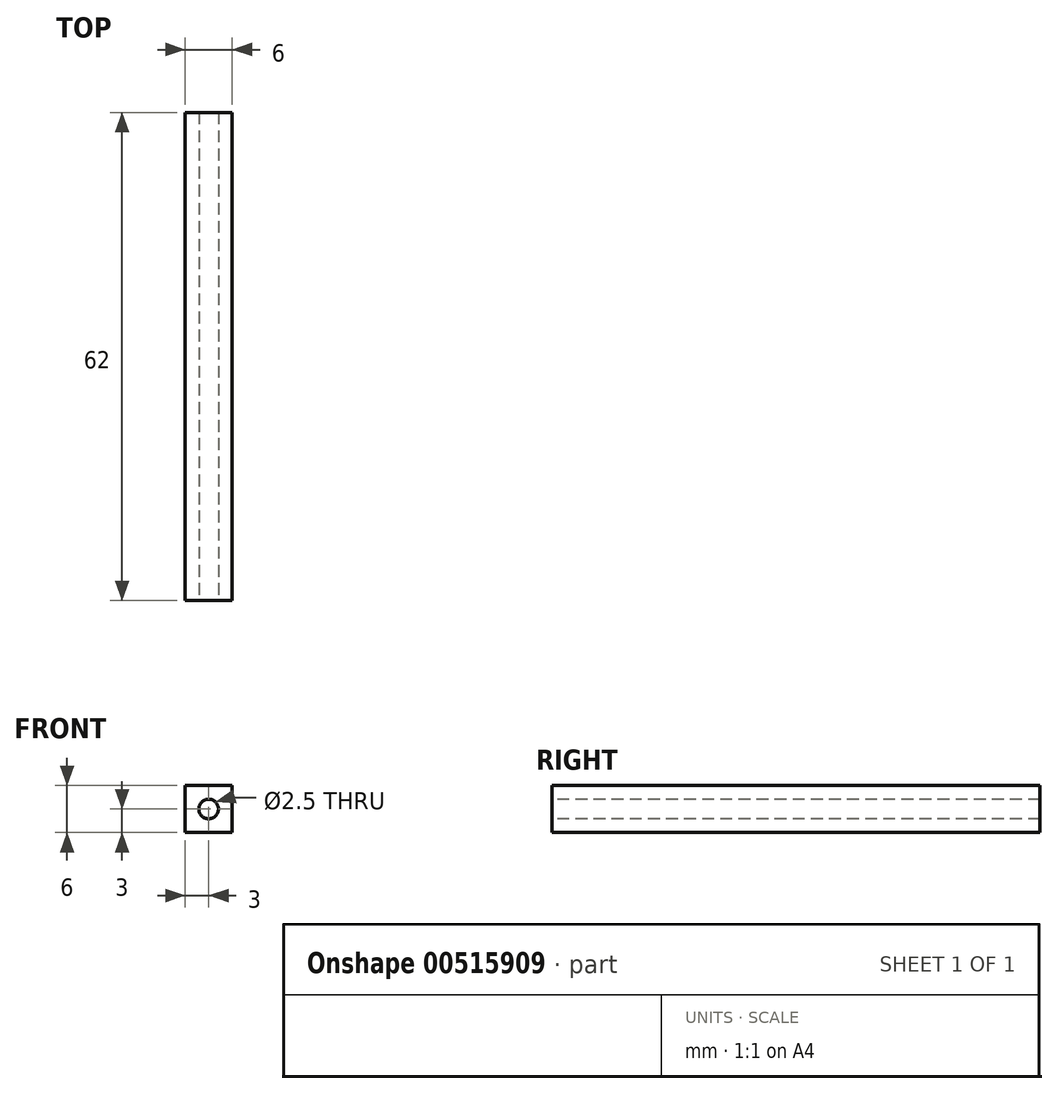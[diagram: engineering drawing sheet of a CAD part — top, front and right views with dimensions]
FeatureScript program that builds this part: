
annotation { "Feature Type Name" : "Feature", "Feature Type Description" : "" }
export const myFeature = defineFeature(function(context is Context, id is Id, definition is map)
    precondition{}
    {
        {
            var Q0;
            Q0=qCreatedBy(makeId("Front.planeOp"),FACE);
            var sketch = newSketch(context, id + "F0", { "sketchPlane" : qUnion([Q0])});
            skLineSegment(sketch, "E0.bottom", {"start": v(3, -3) * mm, "end": v(-3, -3) * mm});
            skLineSegment(sketch, "E0.top", {"start": v(3, 3) * mm, "end": v(-3, 3) * mm});
            skLineSegment(sketch, "E0.left", {"start": v(3, -3) * mm, "end": v(3, 3) * mm});
            skLineSegment(sketch, "E0.right", {"start": v(-3, -3) * mm, "end": v(-3, 3) * mm});
            skPoint(sketch, "E0.middle", {"position": v(0, 0) * mm});
            skSolve(sketch);
        }
        {
            var Q0;
            Q0=makeQuery(id+"F0.imprint","IMPRINT",FACE,{"disambiguationData":[TD([[makeQuery(id+"F0.imprint","IMPRINT",EDGE,{"derivedFrom":sQuery(id+"F0.wireOp",EDGE,"E0.bottom")}),-1.0]])]});
            extrude(context, id + "F1", {"entities" : qUnion([Q0]), "depth" : 62 * mm, "offsetDistance" : 25 * mm});
        }
        {
            var Q0;
            Q0=makeQuery(id+"F1.opExtrude","CAP_FACE",FACE,{"disambiguationData":[OSD([sQuery(id+"F0.wireOp",EDGE,"E0.bottom"),sQuery(id+"F0.wireOp",EDGE,"E0.top"),sQuery(id+"F0.wireOp",EDGE,"E0.left"),sQuery(id+"F0.wireOp",EDGE,"E0.right")])],"isStart":false});
            var sketch = newSketch(context, id + "F2", { "sketchPlane" : qUnion([Q0])});
            skCircle(sketch, "E1", {"center": v(0, 0) * mm, "radius": 1.25 * mm});
            skSolve(sketch);
        }
        {
            var Q0;
            Q0=makeQuery(id+"F2.imprint","IMPRINT",FACE,{"disambiguationData":[TD([[makeQuery(id+"F2.imprint","IMPRINT",EDGE,{"derivedFrom":sQuery(id+"F2.wireOp",EDGE,"E1")}),1.0]])]});
            extrude(context, id + "F3", {"entities" : qUnion([Q0]), "operationType" : NewBodyOperationType.REMOVE, "endBound" : BoundingType.THROUGH_ALL, "oppositeDirection" : true, "depth" : 25 * mm, "offsetDistance" : 25 * mm});
        }
    });
